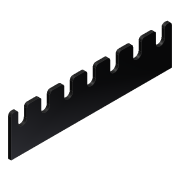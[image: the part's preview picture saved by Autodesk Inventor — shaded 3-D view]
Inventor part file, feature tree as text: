
AUTODESK INVENTOR PART (.ipt)
format: ipt  version: 2012 (Build 160160000, 160)  size: 138,240 bytes
history: native  units: in
note: dims shown in document units (in); Inventor stores cm internally (conversion verified against a paired STEP export)
features: extrude x2, sketch x2, pattern_linear x1, fillet x1
ambient origin geometry x8: Origin, YZ Plane, XZ Plane, XY Plane, X Axis, Y Axis, Z Axis, Center Point
bodies: Solid1 (feature_tree)
feature tree (6):
  extrude  "Extrusion1"  Depth=7.0in TaperAngle=0.0deg
  extrude  "Extrusion3"  Depth=0.5in
  pattern_linear  "Rectangular Pattern1"  Spacing1=0.5in  [1 undecoded]
  fillet  "Fillet1"  Radius=8.0in
  sketch  "Sketch1"  dims[d0=1.75in d2=7.0in d3=0.0in]
  sketch  "Sketch3"  dims[d9=0.375in d10=0.5in d11=0.5in d12=8.0in d13=0.0in d14=2.7559in d16=1.0in d17=0.125in d18=0.125in]
note: 1 required parameter value undecoded (feature->parameter linkage not recoverable at this tier; creation-order binding heuristic only, values carry confidence <= 0.55)
